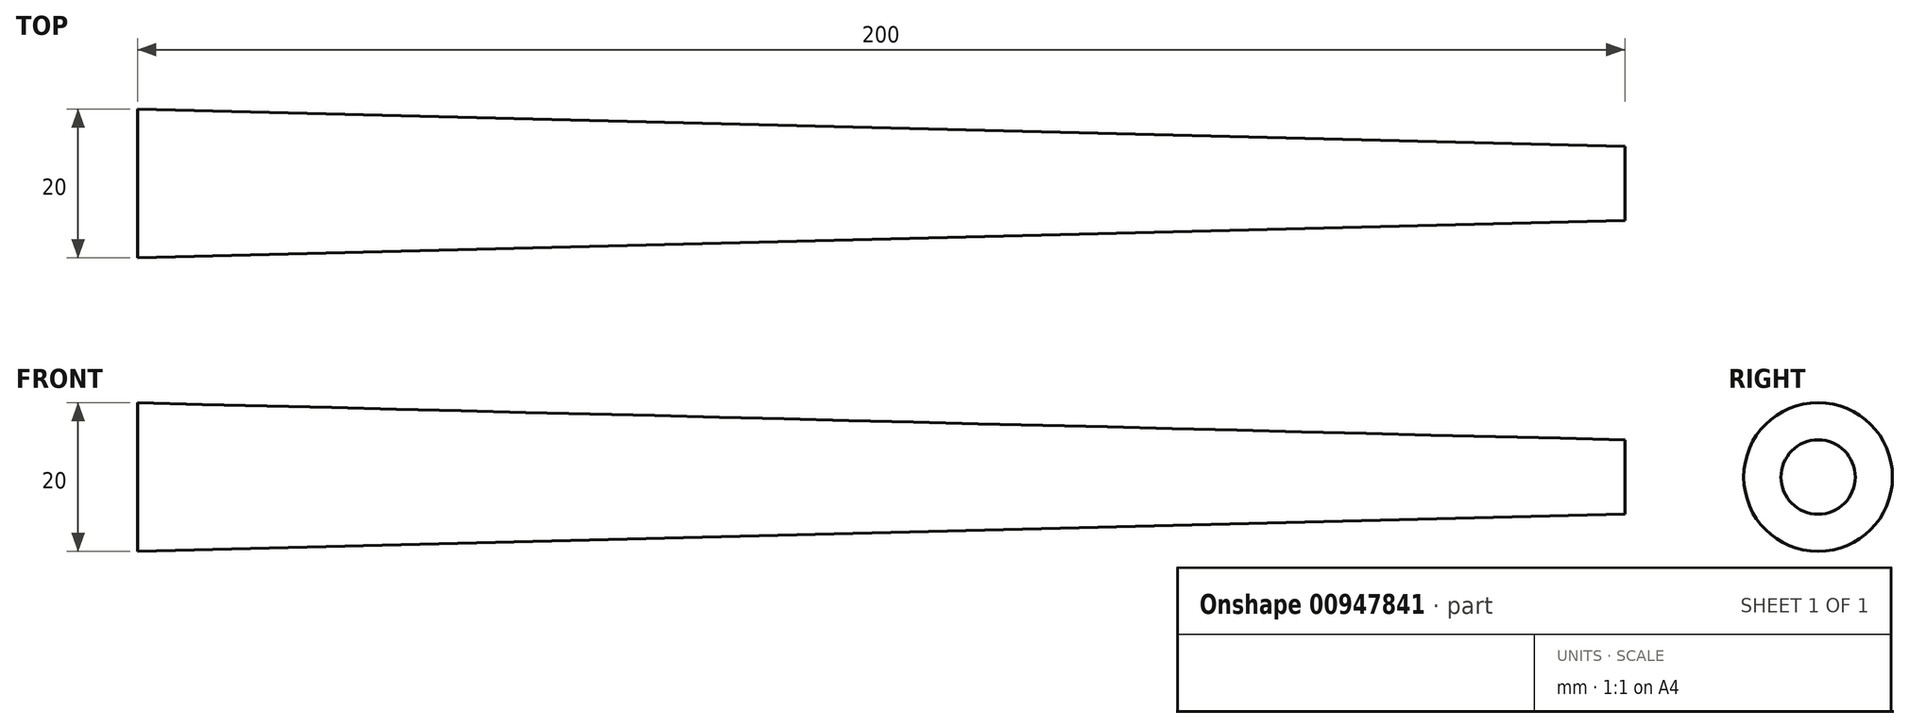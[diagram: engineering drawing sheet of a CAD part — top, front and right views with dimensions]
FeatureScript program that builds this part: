
annotation { "Feature Type Name" : "Feature", "Feature Type Description" : "" }
export const myFeature = defineFeature(function(context is Context, id is Id, definition is map)
    precondition{}
    {
        {
            var Q0;
            Q0=qCreatedBy(makeId("Front.planeOp"),FACE);
            var sketch = newSketch(context, id + "F0", { "sketchPlane" : qUnion([Q0])});
            skLineSegment(sketch, "E0", {"start": v(0, 0) * mm, "end": v(0, 10) * mm});
            skLineSegment(sketch, "E1", {"start": v(0, 10) * mm, "end": v(200, 5) * mm});
            skLineSegment(sketch, "E2", {"start": v(200, 5) * mm, "end": v(200, 0) * mm});
            skLineSegment(sketch, "E3", {"start": v(-35.64, 0) * mm, "end": v(255.15, 0) * mm, "construction": true});
            skLineSegment(sketch, "E4", {"start": v(0, 0) * mm, "end": v(200, 0) * mm});
            skSolve(sketch);
        }
        {
            var Q0;
            Q0 = qSketchRegion(id + "F0", true);
            var Q1;
            Q1=sQuery(id+"F0.wireOp",EDGE,"E3");
            revolve(context, id + "F1", {"surfaceOperationType" : NewSurfaceOperationType.NEW, "entities" : qUnion([Q0]), "axis" : qUnion([Q1]), "revolveType" : RevolveType.FULL});
        }
    });
